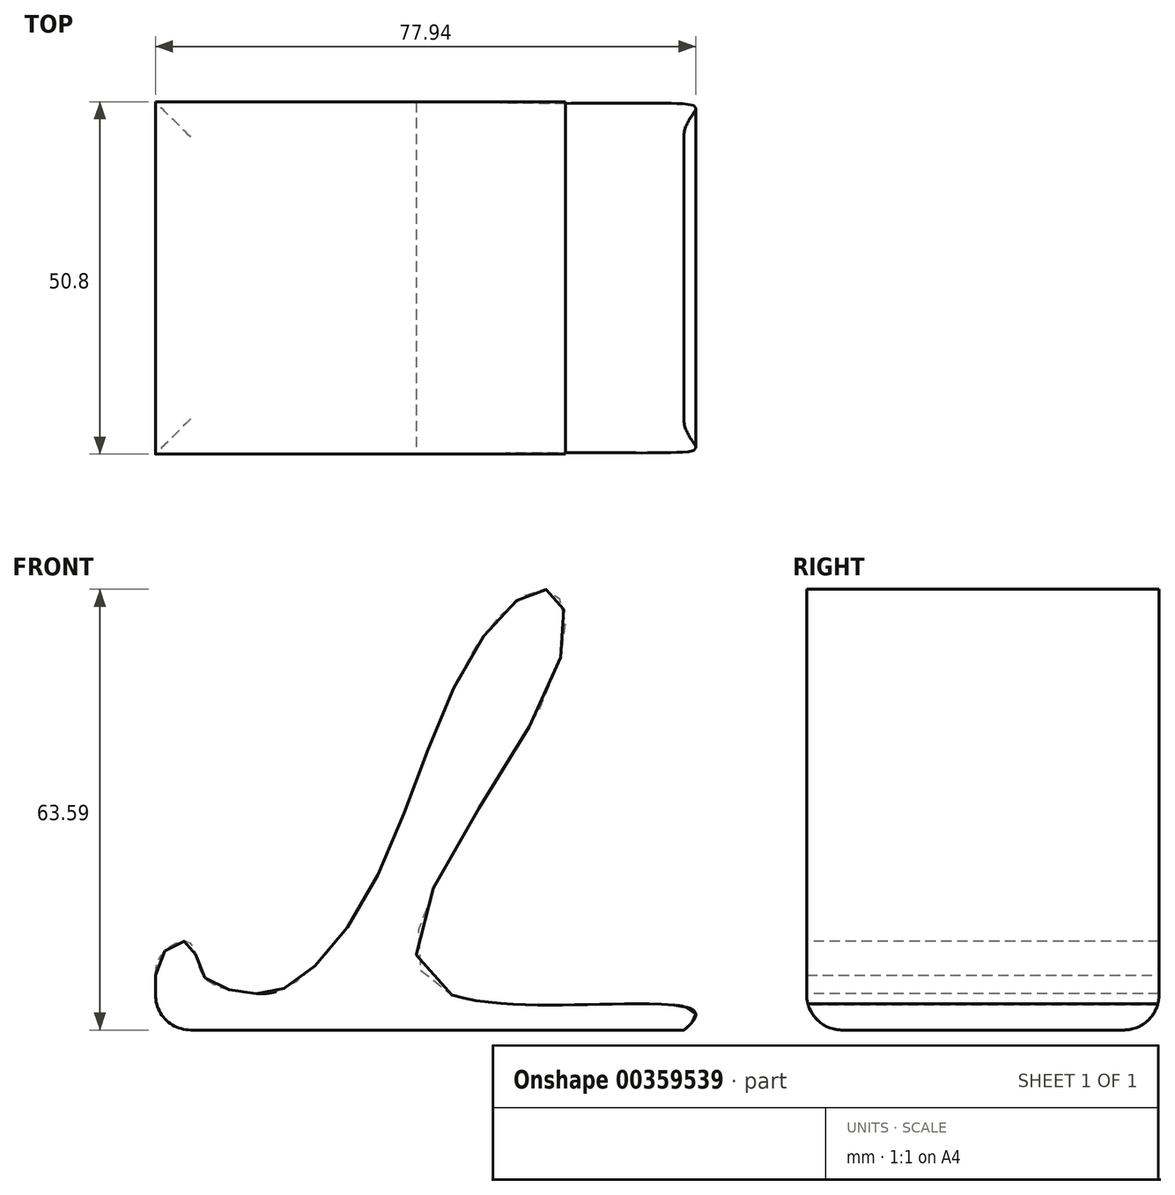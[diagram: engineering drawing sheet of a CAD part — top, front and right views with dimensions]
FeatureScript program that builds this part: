
annotation { "Feature Type Name" : "Feature", "Feature Type Description" : "" }
export const myFeature = defineFeature(function(context is Context, id is Id, definition is map)
    precondition{}
    {
        {
            var Q0;
            Q0=qCreatedBy(makeId("Front.planeOp"),FACE);
            var sketch = newSketch(context, id + "F0", { "sketchPlane" : qUnion([Q0])});
            skLineSegment(sketch, "E0", {"start": v(-76.2, -13.38) * mm, "end": v(-76.2, -21.3) * mm});
            skLineSegment(sketch, "E1", {"start": v(-76.2, -21.3) * mm, "end": v(-58.84, -21.3) * mm});
            skFitSpline(sketch, "E2", {"points": [v(-76.2, -13.38) * mm, v(-73.64, -8.96) * mm, v(-71.04, -8.92) * mm, v(-69.39, -13.38) * mm, v(-63.91, -15.8) * mm, v(-57.58, -15.29) * mm, v(-44.65, 0) * mm, v(-30.19, 33.6) * mm, v(-19.57, 42.2) * mm, v(-19.25, 28.33) * mm, v(-35.27, -15.44) * mm, v(0, -21.3) * mm], "startDerivative": vector(-9.18, 109.98) * mm, "endDerivative": vector(-206.45, -161) * mm});
            skLineSegment(sketch, "E3", {"start": v(0, -21.3) * mm, "end": v(-58.84, -21.3) * mm});
            skSolve(sketch);
        }
        {
            var Q0;
            Q0=makeQuery(id+"F0.imprint","IMPRINT",FACE,{"disambiguationData":[TD([[makeQuery(id+"F0.imprint","IMPRINT",EDGE,{"derivedFrom":sQuery(id+"F0.wireOp",EDGE,"E0")}),1.0]])]});
            extrude(context, id + "F1", {"entities" : qUnion([Q0]), "depth" : 50.8 * mm, "offsetDistance" : 25.4 * mm});
        }
        {
            var Q0;
            Q0=makeQuery(id+"F1.opExtrude","CAP_EDGE",EDGE,{"disambiguationData":[OSD([sQuery(id+"F0.wireOp",EDGE,"E1"),sQuery(id+"F0.wireOp",EDGE,"E3")])],"isStart":false});
            var Q1;
            Q1=makeQuery(id+"F1.opExtrude","CAP_EDGE",EDGE,{"disambiguationData":[OSD([sQuery(id+"F0.wireOp",EDGE,"E1"),sQuery(id+"F0.wireOp",EDGE,"E3")])],"isStart":true});
            var Q2;
            Q2=makeQuery(id+"F1.opExtrude","SWEPT_EDGE",EDGE,{"disambiguationData":[OSD([sQuery(id+"F0.wireOp",EDGE,"E0"),sQuery(id+"F0.wireOp",EDGE,"E1")])]});
            fillet(context, id + "F2", {"entities" : qUnion([Q0, Q1, Q2]), "radius" : 5.08 * mm, "tangentPropagation" : true, "allowEdgeOverflow" : false});
        }
    });
